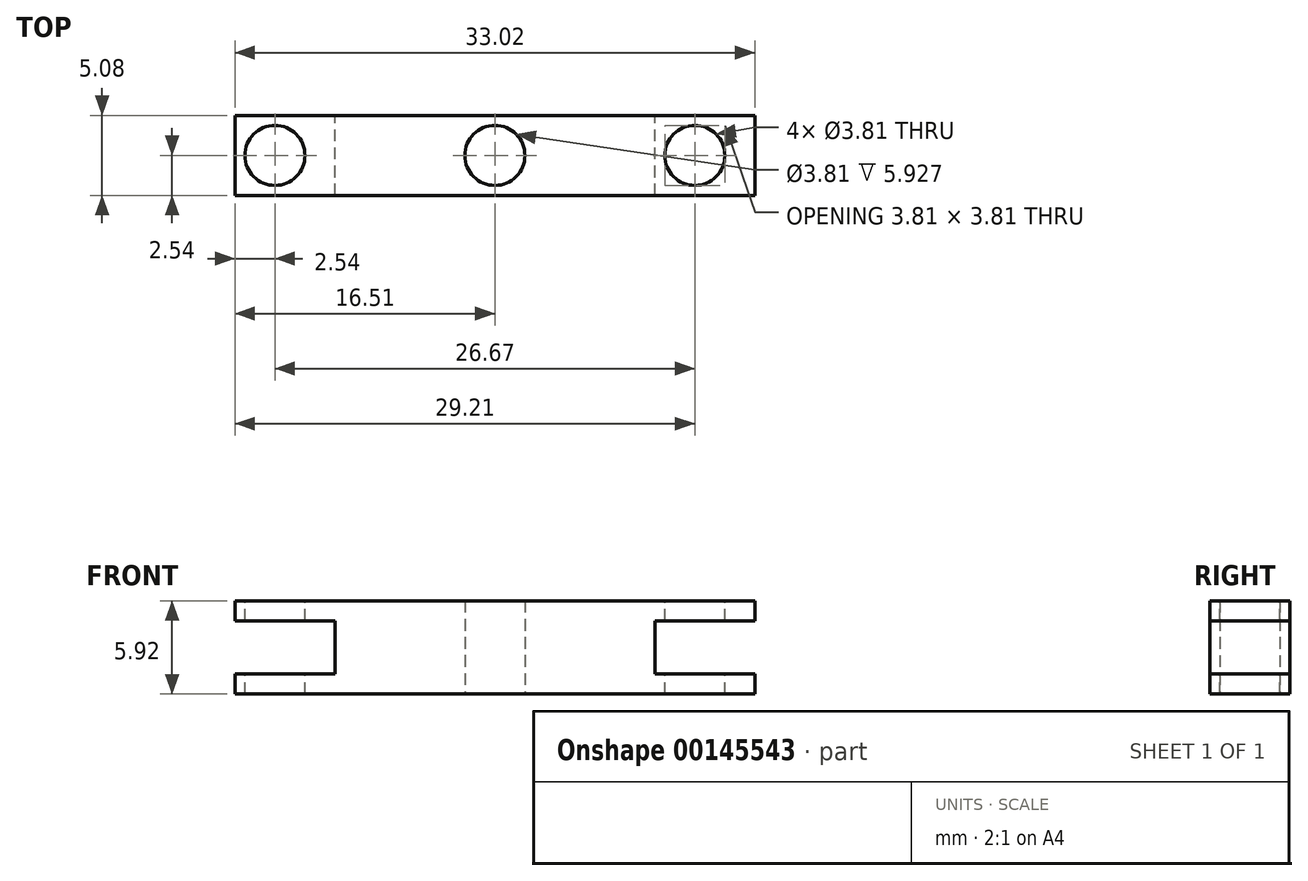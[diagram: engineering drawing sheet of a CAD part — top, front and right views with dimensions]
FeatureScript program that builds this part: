
annotation { "Feature Type Name" : "Feature", "Feature Type Description" : "" }
export const myFeature = defineFeature(function(context is Context, id is Id, definition is map)
    precondition{}
    {
        {
            var Q0;
            Q0=qCreatedBy(makeId("Top.planeOp"),FACE);
            var sketch = newSketch(context, id + "F0", { "sketchPlane" : qUnion([Q0])});
            skLineSegment(sketch, "E0.bottom", {"start": v(-16.51, 2.54) * mm, "end": v(16.51, 2.54) * mm});
            skLineSegment(sketch, "E0.top", {"start": v(-16.51, -2.54) * mm, "end": v(16.51, -2.54) * mm});
            skLineSegment(sketch, "E0.left", {"start": v(-16.51, 2.54) * mm, "end": v(-16.51, -2.54) * mm});
            skLineSegment(sketch, "E0.right", {"start": v(16.51, 2.54) * mm, "end": v(16.51, -2.54) * mm});
            skCircle(sketch, "E1", {"center": v(0, 0) * mm, "radius": 1.9 * mm});
            skCircle(sketch, "E2", {"center": v(0, 0) * mm, "radius": 3.18 * mm});
            skSolve(sketch);
        }
        {
            var Q0;
            {var subQ0=sQuery(id+"F0.wireOp",EDGE,"E0.right");Q0=makeQuery(id+"F0.imprint","IMPRINT",FACE,{"disambiguationData":[TD([[makeQuery(id+"F0.imprint","IMPRINT",EDGE,{"derivedFrom":subQ0}),-1.0]])]});}
            var Q1;
            {var subQ0=sQuery(id+"F0.wireOp",EDGE,"E0.left");Q1=makeQuery(id+"F0.imprint","IMPRINT",FACE,{"disambiguationData":[TD([[makeQuery(id+"F0.imprint","IMPRINT",EDGE,{"derivedFrom":subQ0}),1.0]])]});}
            extrude(context, id + "F1", {"entities" : qUnion([Q0, Q1]), "endBound" : BoundingType.SYMMETRIC, "depth" : 5.92 * mm});
        }
        {
            var Q0;
            {var subQ0=sQuery(id+"F0.wireOp",EDGE,"E2");var subQ1=sQuery(id+"F0.wireOp",EDGE,"E0.bottom");var subQ2=makeQuery(id+"F0.imprint","INTERSECT",VERTEX,{"disambiguationData":[OD(0.0)],"derivedFrom":[subQ1,subQ0]});Q0=makeQuery(id+"F0.imprint","IMPRINT",FACE,{"disambiguationData":[TD([[makeQuery(id+"F0.imprint","IMPRINT",EDGE,{"disambiguationData":[TD([[subQ2,-1.0]])],"derivedFrom":subQ1}),1.0]])]});}
            var Q1;
            Q1=makeQuery(id+"F0.imprint","IMPRINT",FACE,{"disambiguationData":[TD([[makeQuery(id+"F0.imprint","IMPRINT",EDGE,{"derivedFrom":sQuery(id+"F0.wireOp",EDGE,"E1")}),-1.0]])]});
            var Q2;
            {var subQ0=sQuery(id+"F0.wireOp",EDGE,"E2");var subQ1=sQuery(id+"F0.wireOp",EDGE,"E0.top");var subQ2=makeQuery(id+"F0.imprint","INTERSECT",VERTEX,{"disambiguationData":[OD(0.0)],"derivedFrom":[subQ1,subQ0]});Q2=makeQuery(id+"F0.imprint","IMPRINT",FACE,{"disambiguationData":[TD([[makeQuery(id+"F0.imprint","IMPRINT",EDGE,{"disambiguationData":[TD([[subQ2,-1.0]])],"derivedFrom":subQ1}),-1.0]])]});}
            extrude(context, id + "F2", {"entities" : qUnion([Q0, Q1, Q2]), "operationType" : NewBodyOperationType.ADD, "endBound" : BoundingType.SYMMETRIC, "depth" : 5.93 * mm});
        }
        {
            var Q0;
            {var subQ0=sQuery(id+"F0.wireOp",EDGE,"E0.bottom");Q0=makeQuery(id+"F1.opExtrude","SWEPT_FACE",FACE,{"disambiguationData":[OSD([subQ0]),TDD([makeQuery(id+"F0.imprint","IMPRINT",EDGE,{"disambiguationData":[TD([[makeQuery(id+"F0.imprint","INTERSECT",VERTEX,{"derivedFrom":[subQ0,sQuery(id+"F0.wireOp",EDGE,"E0.right")]}),1.0]])],"derivedFrom":subQ0})])]});}
            var sketch = newSketch(context, id + "F3", { "sketchPlane" : qUnion([Q0])});
            skLineSegment(sketch, "E3.bottom", {"start": v(-16.51, -1.69) * mm, "end": v(-10.16, -1.69) * mm});
            skLineSegment(sketch, "E3.top", {"start": v(-16.51, 1.69) * mm, "end": v(-10.16, 1.69) * mm});
            skLineSegment(sketch, "E3.left", {"start": v(-16.51, -1.69) * mm, "end": v(-16.51, 1.69) * mm});
            skLineSegment(sketch, "E3.right", {"start": v(-10.16, -1.69) * mm, "end": v(-10.16, 1.69) * mm});
            skLineSegment(sketch, "E4.bottom", {"start": v(16.51, -1.69) * mm, "end": v(10.16, -1.69) * mm});
            skLineSegment(sketch, "E4.top", {"start": v(16.51, 1.69) * mm, "end": v(10.16, 1.69) * mm});
            skLineSegment(sketch, "E4.left", {"start": v(16.51, -1.69) * mm, "end": v(16.51, 1.69) * mm});
            skLineSegment(sketch, "E4.right", {"start": v(10.16, -1.69) * mm, "end": v(10.16, 1.69) * mm});
            skSolve(sketch);
        }
        {
            var Q0;
            Q0 = qSketchRegion(id + "F3", true);
            extrude(context, id + "F4", {"entities" : qUnion([Q0]), "operationType" : NewBodyOperationType.REMOVE, "endBound" : BoundingType.THROUGH_ALL, "oppositeDirection" : true, "depth" : 25.4 * mm});
        }
        {
            var Q0;
            Q0=makeQuery(id+"F1.opExtrude","CAP_FACE",FACE,{"disambiguationData":[OSD([sQuery(id+"F0.wireOp",EDGE,"E0.bottom"),sQuery(id+"F0.wireOp",EDGE,"E0.top"),sQuery(id+"F0.wireOp",EDGE,"E0.right"),sQuery(id+"F0.wireOp",EDGE,"E2")])],"isStart":false});
            var sketch = newSketch(context, id + "F5", { "sketchPlane" : qUnion([Q0])});
            skCircle(sketch, "E5", {"center": v(12.7, 0) * mm, "radius": 1.9 * mm});
            skCircle(sketch, "E6", {"center": v(-13.97, 0) * mm, "radius": 1.9 * mm});
            skSolve(sketch);
        }
        {
            var Q0;
            Q0 = qSketchRegion(id + "F5", true);
            extrude(context, id + "F6", {"entities" : qUnion([Q0]), "operationType" : NewBodyOperationType.REMOVE, "endBound" : BoundingType.THROUGH_ALL, "oppositeDirection" : true, "depth" : 25.4 * mm});
        }
    });
